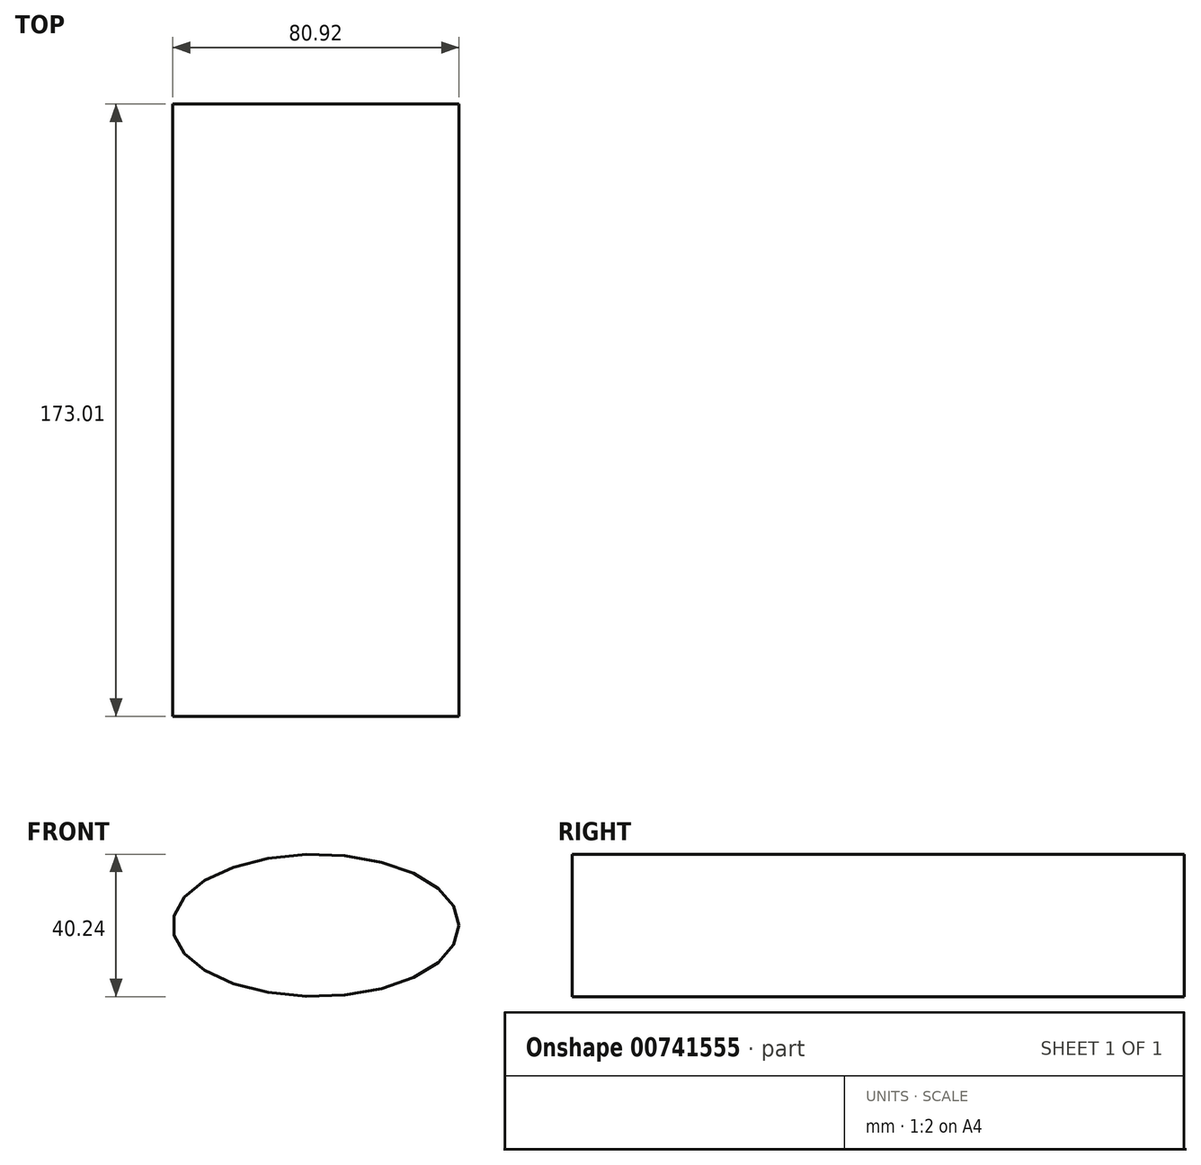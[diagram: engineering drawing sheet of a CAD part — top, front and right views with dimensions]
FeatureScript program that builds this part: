
annotation { "Feature Type Name" : "Feature", "Feature Type Description" : "" }
export const myFeature = defineFeature(function(context is Context, id is Id, definition is map)
    precondition{}
    {
        {
            var Q0;
            Q0=qCreatedBy(makeId("Front.planeOp"),FACE);
            var sketch = newSketch(context, id + "F0", { "sketchPlane" : qUnion([Q0])});
            skEllipse(sketch, "E0", {"center": v(0, 0) * mm, "majorRadius": 20.12 * mm, "minorRadius": 40.46 * mm, "majorAxis": v(0, -1)});
            skFitSpline(sketch, "E1.0", {"points": [v(53.09, -2.27) * mm, v(53.2, 0) * mm, v(53.09, 2.27) * mm, v(52.64, 5.23) * mm, v(51.57, 8.75) * mm, v(49.63, 12.55) * mm, v(47.2, 15.9) * mm, v(44.4, 18.83) * mm, v(41.3, 21.4) * mm, v(38.5, 23.28) * mm, v(36.12, 24.65) * mm, v(34.28, 25.61) * mm, v(32.38, 26.5) * mm, v(29.8, 27.61) * mm, v(26.47, 28.84) * mm, v(22.33, 30.07) * mm, v(18.07, 31.07) * mm, v(13.68, 31.85) * mm, v(9.2, 32.4) * mm, v(5.4, 32.7) * mm, v(2.32, 32.8) * mm, v(0, 32.83) * mm, v(-2.32, 32.8) * mm, v(-5.4, 32.7) * mm, v(-9.2, 32.4) * mm, v(-13.68, 31.85) * mm, v(-18.07, 31.07) * mm, v(-22.33, 30.07) * mm, v(-26.47, 28.84) * mm, v(-29.8, 27.61) * mm, v(-32.38, 26.5) * mm, v(-34.28, 25.61) * mm, v(-36.12, 24.65) * mm, v(-38.5, 23.28) * mm, v(-41.3, 21.4) * mm, v(-44.4, 18.83) * mm, v(-47.2, 15.9) * mm, v(-49.63, 12.55) * mm, v(-51.57, 8.75) * mm, v(-52.64, 5.23) * mm, v(-53.09, 2.27) * mm, v(-53.2, 0) * mm, v(-53.09, -2.27) * mm, v(-52.64, -5.23) * mm, v(-51.57, -8.75) * mm, v(-49.63, -12.55) * mm, v(-47.2, -15.9) * mm, v(-44.4, -18.83) * mm, v(-41.3, -21.4) * mm, v(-38.5, -23.28) * mm, v(-36.12, -24.65) * mm, v(-34.28, -25.61) * mm, v(-32.38, -26.5) * mm, v(-29.8, -27.61) * mm, v(-26.47, -28.84) * mm, v(-22.33, -30.07) * mm, v(-18.07, -31.07) * mm, v(-13.68, -31.85) * mm, v(-9.2, -32.4) * mm, v(-5.4, -32.7) * mm, v(-2.32, -32.8) * mm, v(0, -32.83) * mm, v(2.32, -32.8) * mm, v(5.4, -32.7) * mm, v(9.2, -32.4) * mm, v(13.68, -31.85) * mm, v(18.07, -31.07) * mm, v(22.33, -30.07) * mm, v(26.47, -28.84) * mm, v(29.8, -27.61) * mm, v(32.38, -26.5) * mm, v(34.28, -25.61) * mm, v(36.12, -24.65) * mm, v(38.5, -23.28) * mm, v(41.3, -21.4) * mm, v(44.4, -18.83) * mm, v(47.2, -15.9) * mm, v(49.63, -12.55) * mm, v(51.57, -8.75) * mm, v(52.64, -5.23) * mm, v(53.09, -2.27) * mm, v(53.2, 0) * mm, v(53.09, 2.27) * mm, v(53.09, -2.27) * mm], "construction": true});
            skFitSpline(sketch, "E2.0", {"points": [v(103.95, -1.84) * mm, v(103.97, 0) * mm, v(103.95, 1.84) * mm, v(103.88, 3.66) * mm, v(103.77, 5.48) * mm, v(103.6, 7.3) * mm, v(103.4, 9.1) * mm, v(103.16, 10.9) * mm, v(102.87, 12.67) * mm, v(102.54, 14.43) * mm, v(102.17, 16.17) * mm, v(101.63, 18.46) * mm, v(100.86, 21.25) * mm, v(99.8, 24.49) * mm, v(98.62, 27.64) * mm, v(97.32, 30.67) * mm, v(95.46, 34.54) * mm, v(93.44, 38.15) * mm, v(91.3, 41.51) * mm, v(89.63, 43.91) * mm, v(87.92, 46.2) * mm, v(86.18, 48.36) * mm, v(84.41, 50.4) * mm, v(82.62, 52.36) * mm, v(80.8, 54.2) * mm, v(78.99, 55.95) * mm, v(77.16, 57.6) * mm, v(75.32, 59.18) * mm, v(73.47, 60.67) * mm, v(71.63, 62.08) * mm, v(69.79, 63.42) * mm, v(67.94, 64.7) * mm, v(66.09, 65.9) * mm, v(64.25, 67.05) * mm, v(62.4, 68.14) * mm, v(59.95, 69.52) * mm, v(56.88, 71.12) * mm, v(53.23, 72.85) * mm, v(49.6, 74.4) * mm, v(46, 75.79) * mm, v(41.24, 77.45) * mm, v(35.34, 79.2) * mm, v(28.3, 80.85) * mm, v(21.26, 82.1) * mm, v(15.4, 82.83) * mm, v(10.68, 83.24) * mm, v(7.13, 83.46) * mm, v(3.57, 83.6) * mm, v(0, 83.64) * mm, v(-3.57, 83.6) * mm, v(-7.13, 83.46) * mm, v(-10.68, 83.24) * mm, v(-15.4, 82.83) * mm, v(-21.26, 82.1) * mm, v(-28.3, 80.85) * mm, v(-35.34, 79.2) * mm, v(-41.24, 77.45) * mm, v(-46, 75.79) * mm, v(-49.6, 74.4) * mm, v(-53.23, 72.85) * mm, v(-56.88, 71.12) * mm, v(-59.95, 69.52) * mm, v(-62.4, 68.14) * mm, v(-64.25, 67.05) * mm, v(-66.09, 65.9) * mm, v(-67.94, 64.7) * mm, v(-69.79, 63.42) * mm, v(-71.63, 62.08) * mm, v(-73.47, 60.67) * mm, v(-75.32, 59.18) * mm, v(-77.16, 57.6) * mm, v(-78.99, 55.95) * mm, v(-80.8, 54.2) * mm, v(-82.62, 52.36) * mm, v(-84.41, 50.4) * mm, v(-86.18, 48.36) * mm, v(-87.92, 46.2) * mm, v(-89.63, 43.91) * mm, v(-91.3, 41.51) * mm, v(-93.44, 38.15) * mm, v(-95.46, 34.54) * mm, v(-97.32, 30.67) * mm, v(-98.62, 27.64) * mm, v(-99.8, 24.49) * mm, v(-100.86, 21.25) * mm, v(-101.63, 18.46) * mm, v(-102.17, 16.17) * mm, v(-102.54, 14.43) * mm, v(-102.87, 12.67) * mm, v(-103.16, 10.9) * mm, v(-103.4, 9.1) * mm, v(-103.6, 7.3) * mm, v(-103.77, 5.48) * mm, v(-103.88, 3.66) * mm, v(-103.95, 1.84) * mm, v(-103.97, 0) * mm, v(-103.95, -1.84) * mm, v(-103.88, -3.66) * mm, v(-103.77, -5.48) * mm, v(-103.6, -7.3) * mm, v(-103.4, -9.1) * mm, v(-103.16, -10.9) * mm, v(-102.87, -12.67) * mm, v(-102.54, -14.43) * mm, v(-102.17, -16.17) * mm, v(-101.63, -18.46) * mm, v(-100.86, -21.25) * mm, v(-99.8, -24.49) * mm, v(-98.62, -27.64) * mm, v(-97.32, -30.67) * mm, v(-95.46, -34.54) * mm, v(-93.44, -38.15) * mm, v(-91.3, -41.51) * mm, v(-89.63, -43.91) * mm, v(-87.92, -46.2) * mm, v(-86.18, -48.36) * mm, v(-84.41, -50.4) * mm, v(-82.62, -52.36) * mm, v(-80.8, -54.2) * mm, v(-78.99, -55.95) * mm, v(-77.16, -57.6) * mm, v(-75.32, -59.18) * mm, v(-73.47, -60.67) * mm, v(-71.63, -62.08) * mm, v(-69.79, -63.42) * mm, v(-67.94, -64.7) * mm, v(-66.09, -65.9) * mm, v(-64.25, -67.05) * mm, v(-62.4, -68.14) * mm, v(-59.95, -69.52) * mm, v(-56.88, -71.12) * mm, v(-53.23, -72.85) * mm, v(-49.6, -74.4) * mm, v(-46, -75.79) * mm, v(-41.24, -77.45) * mm, v(-35.34, -79.2) * mm, v(-28.3, -80.85) * mm, v(-21.26, -82.1) * mm, v(-15.4, -82.83) * mm, v(-10.68, -83.24) * mm, v(-7.13, -83.46) * mm, v(-3.57, -83.6) * mm, v(0, -83.64) * mm, v(3.57, -83.6) * mm, v(7.13, -83.46) * mm, v(10.68, -83.24) * mm, v(15.4, -82.83) * mm, v(21.26, -82.1) * mm, v(28.3, -80.85) * mm, v(35.34, -79.2) * mm, v(41.24, -77.45) * mm, v(46, -75.79) * mm, v(49.6, -74.4) * mm, v(53.23, -72.85) * mm, v(56.88, -71.12) * mm, v(59.95, -69.52) * mm, v(62.4, -68.14) * mm, v(64.25, -67.05) * mm, v(66.09, -65.9) * mm, v(67.94, -64.7) * mm, v(69.79, -63.42) * mm, v(71.63, -62.08) * mm, v(73.47, -60.67) * mm, v(75.32, -59.18) * mm, v(77.16, -57.6) * mm, v(78.99, -55.95) * mm, v(80.8, -54.2) * mm, v(82.62, -52.36) * mm, v(84.41, -50.4) * mm, v(86.18, -48.36) * mm, v(87.92, -46.2) * mm, v(89.63, -43.91) * mm, v(91.3, -41.51) * mm, v(93.44, -38.15) * mm, v(95.46, -34.54) * mm, v(97.32, -30.67) * mm, v(98.62, -27.64) * mm, v(99.8, -24.49) * mm, v(100.86, -21.25) * mm, v(101.63, -18.46) * mm, v(102.17, -16.17) * mm, v(102.54, -14.43) * mm, v(102.87, -12.67) * mm, v(103.16, -10.9) * mm, v(103.4, -9.1) * mm, v(103.6, -7.3) * mm, v(103.77, -5.48) * mm, v(103.88, -3.66) * mm, v(103.95, -1.84) * mm, v(103.97, 0) * mm, v(103.95, 1.84) * mm, v(103.95, -1.84) * mm]});
            skSolve(sketch);
        }
        {
            var Q0;
            Q0 = qSketchRegion(id + "F0", true);
            extrude(context, id + "F1", {"entities" : qUnion([Q0]), "depth" : 173 * mm, "offsetDistance" : 25.4 * mm});
        }
    });
